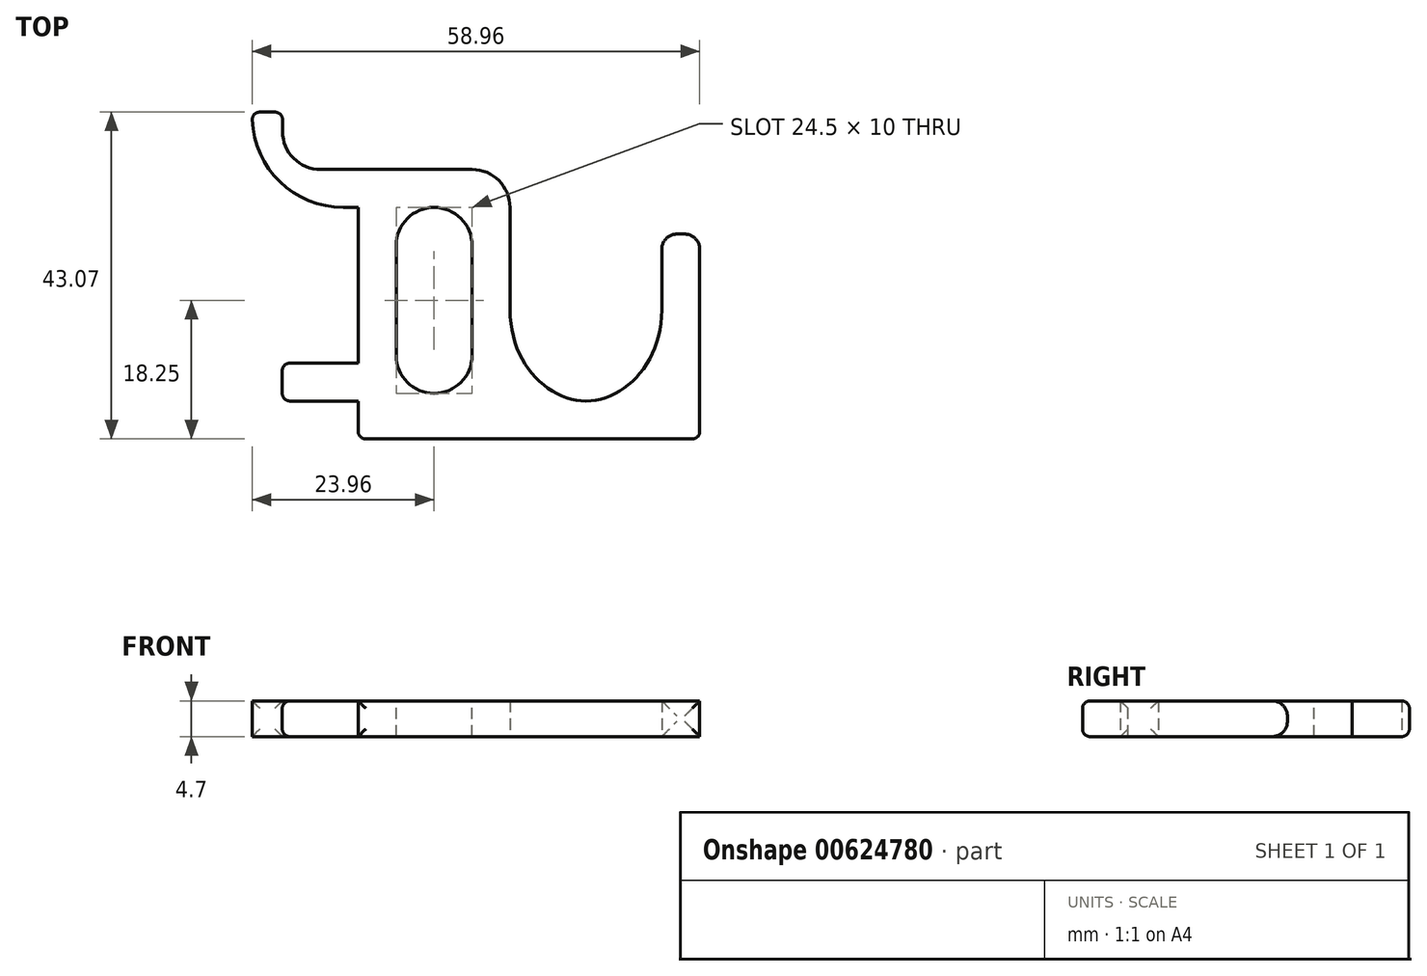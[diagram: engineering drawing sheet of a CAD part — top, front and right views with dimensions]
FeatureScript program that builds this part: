
annotation { "Feature Type Name" : "Feature", "Feature Type Description" : "" }
export const myFeature = defineFeature(function(context is Context, id is Id, definition is map)
    precondition{}
    {
        {
            var Q0;
            Q0=qCreatedBy(makeId("Top.planeOp"),FACE);
            var sketch = newSketch(context, id + "F0", { "sketchPlane" : qUnion([Q0])});
            skLineSegment(sketch, "E0", {"start": v(-13.96, 33.07) * mm, "end": v(-9.96, 33.07) * mm});
            skLineSegment(sketch, "E1", {"start": v(20, 20.5) * mm, "end": v(20, -10) * mm});
            skLineSegment(sketch, "E2", {"start": v(20, -10) * mm, "end": v(0, -10) * mm});
            skLineSegment(sketch, "E3", {"start": v(0, -10) * mm, "end": v(0, -5) * mm});
            skLineSegment(sketch, "E4", {"start": v(0, -5) * mm, "end": v(-10, -5) * mm});
            skLineSegment(sketch, "E5", {"start": v(-10, -5) * mm, "end": v(-10, 0) * mm});
            skLineSegment(sketch, "E6", {"start": v(-10, 0) * mm, "end": v(0, 0) * mm});
            skLineSegment(sketch, "E7", {"start": v(0, 0) * mm, "end": v(0, 20.5) * mm});
            skFitSpline(sketch, "E8", {"points": [v(20, 7) * mm, v(30, -5) * mm, v(40, 7) * mm], "startDerivative": vector(0, -42) * mm, "endDerivative": vector(0, 42) * mm});
            skLineSegment(sketch, "E9.bottom", {"start": v(20, -10) * mm, "end": v(40, -10) * mm});
            skLineSegment(sketch, "E9.top", {"start": v(20, -5) * mm, "end": v(40, -5) * mm});
            skLineSegment(sketch, "E9.left", {"start": v(20, -10) * mm, "end": v(20, -5) * mm});
            skLineSegment(sketch, "E9.right", {"start": v(40, -10) * mm, "end": v(40, -5) * mm});
            skLineSegment(sketch, "E10", {"start": v(40, -5) * mm, "end": v(40, 7) * mm});
            skLineSegment(sketch, "E11.bottom", {"start": v(40, 7) * mm, "end": v(45, 7) * mm});
            skLineSegment(sketch, "E11.top", {"start": v(40, -10) * mm, "end": v(45, -10) * mm});
            skLineSegment(sketch, "E11.left", {"start": v(40, 7) * mm, "end": v(40, -10) * mm});
            skLineSegment(sketch, "E11.right", {"start": v(45, 7) * mm, "end": v(45, -10) * mm});
            skLineSegment(sketch, "E12", {"start": v(20, 20.5) * mm, "end": v(20, 25.5) * mm});
            skLineSegment(sketch, "E13", {"start": v(20, 25.5) * mm, "end": v(0, 25.5) * mm});
            skLineSegment(sketch, "E14", {"start": v(0, 20.5) * mm, "end": v(-13.96, 20.5) * mm});
            skLineSegment(sketch, "E15", {"start": v(-13.96, 20.5) * mm, "end": v(-13.96, 33.07) * mm});
            skLineSegment(sketch, "E16", {"start": v(0, 25.5) * mm, "end": v(-9.96, 25.5) * mm});
            skLineSegment(sketch, "E17", {"start": v(-9.96, 25.5) * mm, "end": v(-9.96, 33.07) * mm});
            skSolve(sketch);
        }
        {
            var Q0;
            Q0=qSketchRegion(id+"F0",true);
            extrude(context, id + "F1", {"entities" : qUnion([Q0]), "depth" : 4.7 * mm, "offsetDistance" : 25 * mm});
        }
        {
            var Q0;
            Q0=makeQuery(id+"F1.opExtrude","SWEPT_FACE",FACE,{"disambiguationData":[OSD([sQuery(id+"F0.wireOp",EDGE,"E0")])]});
            fillet(context, id + "F2", {"entities" : qUnion([Q0]), "radius" : 1 * mm, "tangentPropagation" : true, "allowEdgeOverflow" : false});
        }
        {
            var Q0;
            Q0=makeQuery(id+"F1.opExtrude","SWEPT_FACE",FACE,{"disambiguationData":[OSD([sQuery(id+"F0.wireOp",EDGE,"E5")])]});
            fillet(context, id + "F3", {"entities" : qUnion([Q0]), "radius" : 1 * mm, "tangentPropagation" : true, "allowEdgeOverflow" : false});
        }
        {
            var Q0;
            Q0=makeQuery(id+"F1.opExtrude","SWEPT_FACE",FACE,{"disambiguationData":[OSD([sQuery(id+"F0.wireOp",EDGE,"E2")])]});
            fillet(context, id + "F4", {"entities" : qUnion([Q0]), "radius" : 1 * mm, "tangentPropagation" : true, "allowEdgeOverflow" : false});
        }
        {
            var Q0;
            Q0=makeQuery(id+"F1.opExtrude","SWEPT_FACE",FACE,{"disambiguationData":[OSD([sQuery(id+"F0.wireOp",EDGE,"E11.bottom")])]});
            extrude(context, id + "F5", {"entities" : qUnion([Q0]), "operationType" : NewBodyOperationType.ADD, "depth" : 10 * mm, "offsetDistance" : 25 * mm});
        }
        {
            var Q0;
            Q0=makeQuery(id+"F5.opExtrude","CAP_FACE",FACE,{"disambiguationData":[OSD([sQuery(id+"F0.wireOp",EDGE,"E11.bottom")])],"isStart":false});
            fillet(context, id + "F6", {"entities" : qUnion([Q0]), "radius" : 2 * mm, "tangentPropagation" : true, "allowEdgeOverflow" : false});
        }
        {
            var Q0;
            Q0=makeQuery(id+"F1.opExtrude","SWEPT_EDGE",EDGE,{"disambiguationData":[OSD([sQuery(id+"F0.wireOp",EDGE,"E14"),sQuery(id+"F0.wireOp",EDGE,"E15")])]});
            fillet(context, id + "F7", {"entities" : qUnion([Q0]), "radius" : 12 * mm, "tangentPropagation" : true, "allowEdgeOverflow" : false});
        }
        {
            var Q0;
            Q0=makeQuery(id+"F1.opExtrude","SWEPT_EDGE",EDGE,{"disambiguationData":[OSD([sQuery(id+"F0.wireOp",EDGE,"E16"),sQuery(id+"F0.wireOp",EDGE,"E17")])]});
            var Q1;
            Q1=makeQuery(id+"F1.opExtrude","SWEPT_EDGE",EDGE,{"disambiguationData":[OSD([sQuery(id+"F0.wireOp",EDGE,"E12"),sQuery(id+"F0.wireOp",EDGE,"E13")])]});
            fillet(context, id + "F8", {"entities" : qUnion([Q0, Q1]), "radius" : 5 * mm, "tangentPropagation" : true, "allowEdgeOverflow" : false});
        }
        {
            var Q0;
            Q0=qCreatedBy(makeId("Top.planeOp"),FACE);
            var sketch = newSketch(context, id + "F9", { "sketchPlane" : qUnion([Q0])});
            skLineSegment(sketch, "E18.bottom", {"start": v(5, 20.5) * mm, "end": v(15, 20.5) * mm});
            skLineSegment(sketch, "E18.top", {"start": v(5, -4) * mm, "end": v(15, -4) * mm});
            skLineSegment(sketch, "E18.left", {"start": v(5, 20.5) * mm, "end": v(5, -4) * mm});
            skLineSegment(sketch, "E18.right", {"start": v(15, 20.5) * mm, "end": v(15, -4) * mm});
            skSolve(sketch);
        }
        {
            var Q0;
            Q0 = qSketchRegion(id + "F9", true);
            extrude(context, id + "F10", {"entities" : qUnion([Q0]), "operationType" : NewBodyOperationType.REMOVE, "endBound" : BoundingType.SYMMETRIC, "oppositeDirection" : true, "depth" : 25 * mm, "offsetDistance" : 25 * mm});
        }
        {
            var Q0;
            Q0=makeQuery(id+"F10.boolean.opBoolean","COPY",EDGE,{"derivedFrom":makeQuery(id+"F10.opExtrude","SWEPT_EDGE",EDGE,{"disambiguationData":[OSD([sQuery(id+"F9.wireOp",EDGE,"E18.bottom"),sQuery(id+"F9.wireOp",EDGE,"E18.right")])]})});
            var Q1;
            Q1=makeQuery(id+"F10.boolean.opBoolean","COPY",EDGE,{"derivedFrom":makeQuery(id+"F10.opExtrude","SWEPT_EDGE",EDGE,{"disambiguationData":[OSD([sQuery(id+"F9.wireOp",EDGE,"E18.bottom"),sQuery(id+"F9.wireOp",EDGE,"E18.left")])]})});
            var Q2;
            Q2=makeQuery(id+"F10.boolean.opBoolean","COPY",EDGE,{"derivedFrom":makeQuery(id+"F10.opExtrude","SWEPT_EDGE",EDGE,{"disambiguationData":[OSD([sQuery(id+"F9.wireOp",EDGE,"E18.top"),sQuery(id+"F9.wireOp",EDGE,"E18.right")])]})});
            var Q3;
            Q3=makeQuery(id+"F10.boolean.opBoolean","COPY",EDGE,{"derivedFrom":makeQuery(id+"F10.opExtrude","SWEPT_EDGE",EDGE,{"disambiguationData":[OSD([sQuery(id+"F9.wireOp",EDGE,"E18.top"),sQuery(id+"F9.wireOp",EDGE,"E18.left")])]})});
            fillet(context, id + "F11", {"entities" : qUnion([Q0, Q1, Q2, Q3]), "radius" : 5 * mm, "tangentPropagation" : true, "allowEdgeOverflow" : false});
        }
    });
